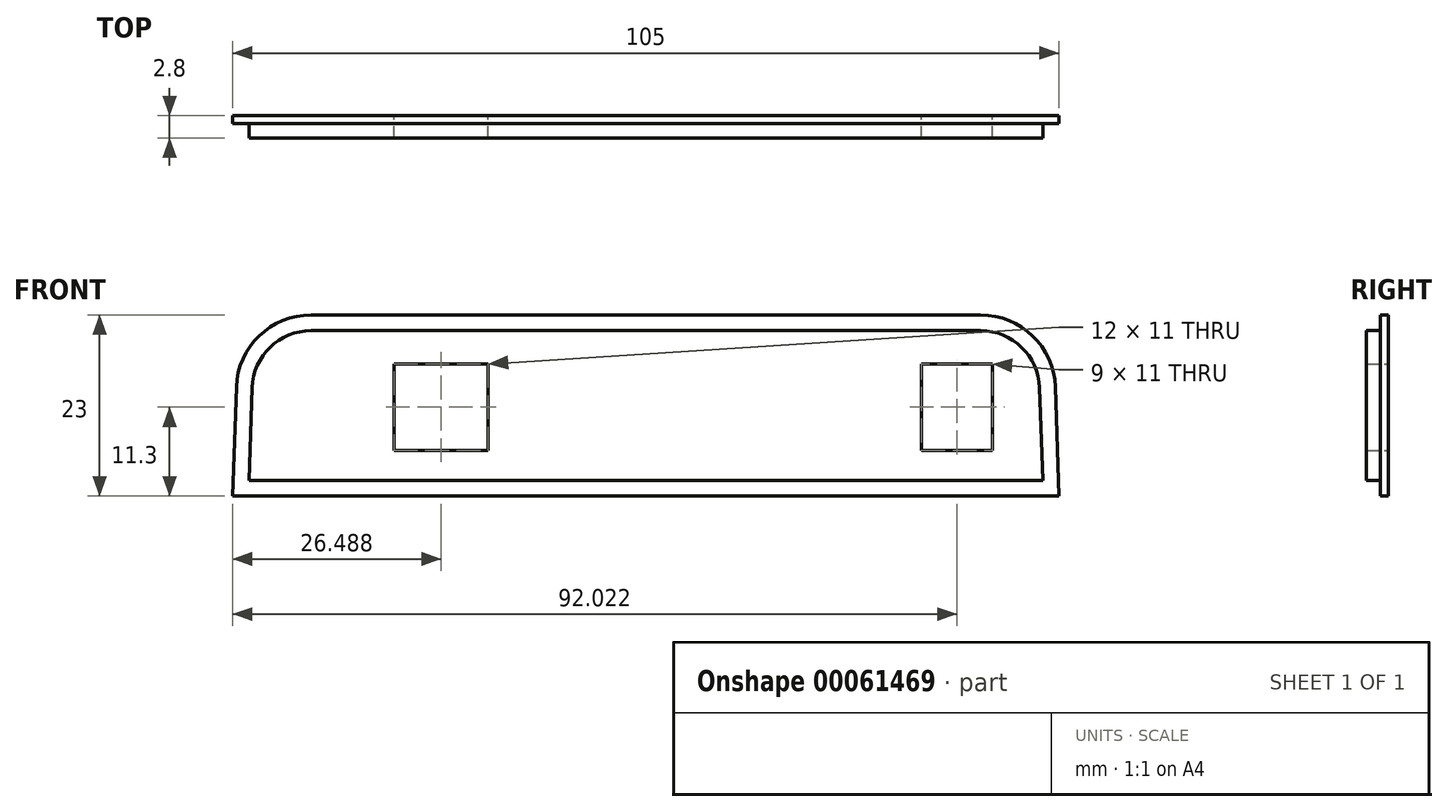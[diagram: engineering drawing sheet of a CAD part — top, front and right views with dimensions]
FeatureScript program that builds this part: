
annotation { "Feature Type Name" : "Feature", "Feature Type Description" : "" }
export const myFeature = defineFeature(function(context is Context, id is Id, definition is map)
    precondition{}
    {
        {
            var Q0;
            Q0=qCreatedBy(makeId("Front.planeOp"),FACE);
            var sketch = newSketch(context, id + "F0", { "sketchPlane" : qUnion([Q0])});
            skLineSegment(sketch, "E0", {"start": v(-48.99, 0) * mm, "end": v(56.01, 0) * mm});
            skLineSegment(sketch, "E1", {"start": v(-48.99, 0) * mm, "end": v(-48.5, 13.83) * mm});
            skLineSegment(sketch, "E2", {"start": v(-39, 23) * mm, "end": v(46.04, 23) * mm});
            skLineSegment(sketch, "E3", {"start": v(55.53, 13.83) * mm, "end": v(56.01, 0) * mm});
            skPoint(sketch, "E4.visualSharp", {"position": v(-48.18, 23) * mm});
            skArc(sketch, "E4.filletArc", {"start": v(-39, 23) * mm, "mid": v(-45.6, 20.33) * mm, "end": v(-48.5, 13.83) * mm});
            skPoint(sketch, "E5.visualSharp", {"position": v(55.21, 23) * mm});
            skArc(sketch, "E5.filletArc", {"start": v(55.53, 13.83) * mm, "mid": v(52.64, 20.33) * mm, "end": v(46.04, 23) * mm});
            skSolve(sketch);
        }
        {
            var Q0;
            Q0=qSketchRegion(id+"F0",true);
            extrude(context, id + "F1", {"entities" : qUnion([Q0]), "depth" : 1 * mm});
        }
        {
            var Q0;
            Q0=makeQuery(id+"F1.opExtrude","CAP_FACE",FACE,{"disambiguationData":[OSD([sQuery(id+"F0.wireOp",EDGE,"E0"),sQuery(id+"F0.wireOp",EDGE,"E1"),sQuery(id+"F0.wireOp",EDGE,"E2"),sQuery(id+"F0.wireOp",EDGE,"E3"),sQuery(id+"F0.wireOp",EDGE,"E4.filletArc"),sQuery(id+"F0.wireOp",EDGE,"E5.filletArc")])],"isStart":false});
            var sketch = newSketch(context, id + "F2", { "sketchPlane" : qUnion([Q0])});
            skLineSegment(sketch, "E6.0", {"start": v(-39, 21) * mm, "end": v(46.04, 21) * mm});
            skArc(sketch, "E6.1", {"start": v(-39, 21) * mm, "mid": v(-44.22, 18.9) * mm, "end": v(-46.5, 13.76) * mm});
            skLineSegment(sketch, "E6.2", {"start": v(-46.91, 2) * mm, "end": v(-46.5, 13.76) * mm});
            skLineSegment(sketch, "E6.3", {"start": v(-46.91, 2) * mm, "end": v(53.94, 2) * mm});
            skLineSegment(sketch, "E7.0", {"start": v(53.53, 13.76) * mm, "end": v(53.94, 2) * mm});
            skArc(sketch, "E7.1", {"start": v(53.53, 13.76) * mm, "mid": v(51.25, 18.9) * mm, "end": v(46.04, 21) * mm});
            skSolve(sketch);
        }
        {
            var Q0;
            Q0=qSketchRegion(id+"F2",true);
            extrude(context, id + "F3", {"entities" : qUnion([Q0]), "operationType" : NewBodyOperationType.ADD, "depth" : 1.8 * mm});
        }
        {
            var Q0;
            Q0=makeQuery(id+"F1.opExtrude","CAP_FACE",FACE,{"disambiguationData":[OSD([sQuery(id+"F0.wireOp",EDGE,"E0"),sQuery(id+"F0.wireOp",EDGE,"E1"),sQuery(id+"F0.wireOp",EDGE,"E2"),sQuery(id+"F0.wireOp",EDGE,"E3"),sQuery(id+"F0.wireOp",EDGE,"E4.filletArc"),sQuery(id+"F0.wireOp",EDGE,"E5.filletArc")])],"isStart":true});
            var sketch = newSketch(context, id + "F4", { "sketchPlane" : qUnion([Q0])});
            skLineSegment(sketch, "E8.bottom", {"start": v(-47.53, 16.8) * mm, "end": v(-38.53, 16.8) * mm});
            skLineSegment(sketch, "E8.top", {"start": v(-47.53, 5.8) * mm, "end": v(-38.53, 5.8) * mm});
            skLineSegment(sketch, "E8.left", {"start": v(-47.53, 16.8) * mm, "end": v(-47.53, 5.8) * mm});
            skLineSegment(sketch, "E8.right", {"start": v(-38.53, 16.8) * mm, "end": v(-38.53, 5.8) * mm});
            skLineSegment(sketch, "E9.bottom", {"start": v(16.5, 16.8) * mm, "end": v(28.5, 16.8) * mm});
            skLineSegment(sketch, "E9.top", {"start": v(16.5, 5.8) * mm, "end": v(28.5, 5.8) * mm});
            skLineSegment(sketch, "E9.left", {"start": v(16.5, 16.8) * mm, "end": v(16.5, 5.8) * mm});
            skLineSegment(sketch, "E9.right", {"start": v(28.5, 16.8) * mm, "end": v(28.5, 5.8) * mm});
            skSolve(sketch);
        }
        {
            var Q0;
            Q0 = qSketchRegion(id + "F4", true);
            extrude(context, id + "F5", {"entities" : qUnion([Q0]), "operationType" : NewBodyOperationType.REMOVE, "endBound" : BoundingType.THROUGH_ALL, "oppositeDirection" : true, "depth" : 25 * mm});
        }
    });
